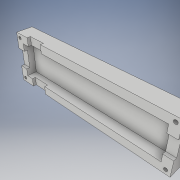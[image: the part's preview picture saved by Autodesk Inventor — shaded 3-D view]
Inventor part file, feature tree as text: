
AUTODESK INVENTOR PART (.ipt)
format: ipt  version: 2019 (Build 230136000, 136)  size: 169,984 bytes
history: native  units: mm
features: sketch x4, extrude x3, projected_geometry x3, mirror x2, hole x1
ambient origin geometry x8: Origin, YZ Plane, XZ Plane, XY Plane, X Axis, Y Axis, Z Axis, Center Point
bodies: Solid1 (feature_tree)
feature tree (13):
  extrude  "Extrusion1"  Depth=30.0mm
  extrude  "Extrusion2"  Depth=5.0mm
  extrude  "Extrusion3"  Depth=11.0mm
  hole  "Hole1"  [1 undecoded]
  mirror  "Mirror1"
  mirror  "Mirror2"
  sketch  "Sketch1"  dims[d0=100.0mm d1=30.0mm]
  sketch  "Sketch2"  dims[d2=10.0mm d3=0.0mm d4=5.0mm]
  projected_geometry  "Projected Loop1"
  sketch  "Sketch3"  dims[d5=6.0mm d6=0.0mm d7=11.0mm]
  projected_geometry  "Projected Loop2"
  sketch  "Sketch4"  dims[d9=11.0mm d10=15.0mm d11=2.0mm d12=0.0mm d16=2.5mm d17=2.5mm d18=2.013mm d19=5.0mm d20=4.0mm d21=2.0mm d22=90.0deg d23=7.6mm d24=20.594885mm d28=11.0mm d29=11.0mm]
  projected_geometry  "Projected Loop3"
note: 1 required parameter value undecoded (feature->parameter linkage not recoverable at this tier; creation-order binding heuristic only, values carry confidence <= 0.55)
